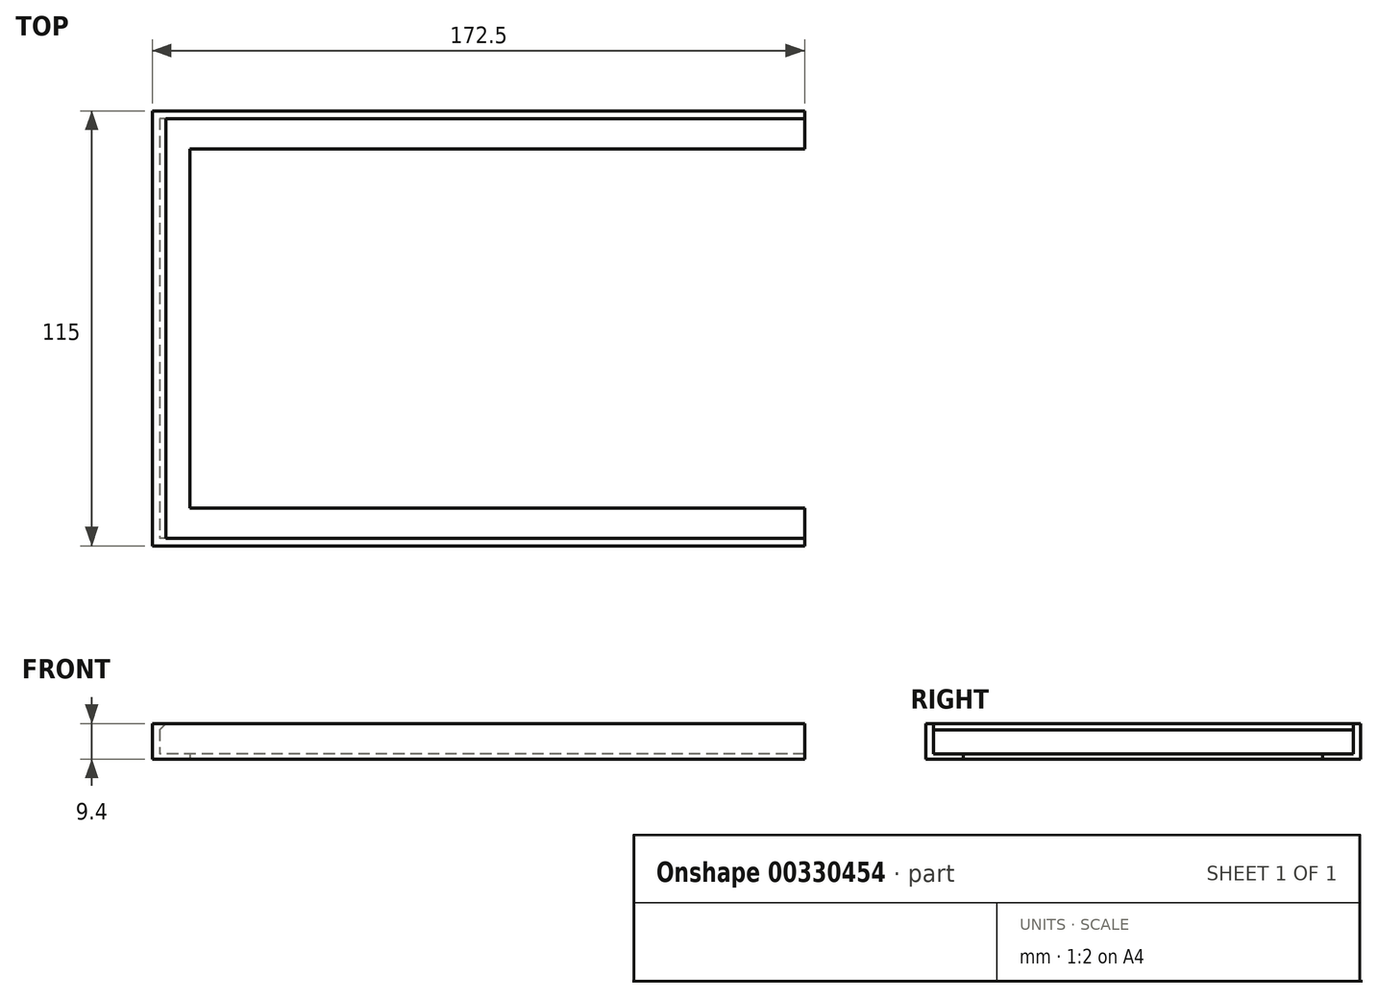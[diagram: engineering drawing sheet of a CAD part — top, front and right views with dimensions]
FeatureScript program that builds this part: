
annotation { "Feature Type Name" : "Feature", "Feature Type Description" : "" }
export const myFeature = defineFeature(function(context is Context, id is Id, definition is map)
    precondition{}
    {
        {
            var Q0;
            Q0=qCreatedBy(makeId("Top.planeOp"),FACE);
            var sketch = newSketch(context, id + "F0", { "sketchPlane" : qUnion([Q0])});
            skLineSegment(sketch, "E0.bottom", {"start": v(86.25, 57.5) * mm, "end": v(-86.25, 57.5) * mm});
            skLineSegment(sketch, "E0.top", {"start": v(86.25, -57.5) * mm, "end": v(-86.25, -57.5) * mm});
            skLineSegment(sketch, "E0.left", {"start": v(86.25, 57.5) * mm, "end": v(86.25, -57.5) * mm});
            skLineSegment(sketch, "E0.right", {"start": v(-86.25, 57.5) * mm, "end": v(-86.25, -57.5) * mm});
            skPoint(sketch, "E0.middle", {"position": v(0, 0) * mm});
            skLineSegment(sketch, "E1.0", {"start": v(86.25, -47.5) * mm, "end": v(-76.25, -47.5) * mm});
            skLineSegment(sketch, "E1.1", {"start": v(-76.25, 47.5) * mm, "end": v(-76.25, -47.5) * mm});
            skLineSegment(sketch, "E1.2", {"start": v(86.25, 47.5) * mm, "end": v(-76.25, 47.5) * mm});
            skLineSegment(sketch, "E2.bottom", {"start": v(-16.25, -47.5) * mm, "end": v(-11.25, -47.5) * mm});
            skLineSegment(sketch, "E2.top", {"start": v(-16.25, 47.5) * mm, "end": v(-11.25, 47.5) * mm});
            skLineSegment(sketch, "E2.left", {"start": v(-16.25, -47.5) * mm, "end": v(-16.25, 47.5) * mm});
            skLineSegment(sketch, "E2.right", {"start": v(-11.25, -47.5) * mm, "end": v(-11.25, 47.5) * mm});
            skLineSegment(sketch, "E3.bottom", {"start": v(48.75, -47.5) * mm, "end": v(53.75, -47.5) * mm});
            skLineSegment(sketch, "E3.top", {"start": v(48.75, 47.5) * mm, "end": v(53.75, 47.5) * mm});
            skLineSegment(sketch, "E3.left", {"start": v(48.75, -47.5) * mm, "end": v(48.75, 47.5) * mm});
            skLineSegment(sketch, "E3.right", {"start": v(53.75, -47.5) * mm, "end": v(53.75, 47.5) * mm});
            skSolve(sketch);
        }
        {
            var Q0;
            {var subQ3=sQuery(id+"F0.wireOp",EDGE,"E0.bottom");Q0=makeQuery(id+"F0.imprint","IMPRINT",FACE,{"disambiguationData":[TD([[makeQuery(id+"F0.imprint","IMPRINT",EDGE,{"derivedFrom":subQ3}),1.0]])]});}
            var Q1;
            Q1=makeQuery(id+"F0.imprint","IMPRINT",FACE,{"disambiguationData":[TD([[makeQuery(id+"F0.imprint","IMPRINT",EDGE,{"derivedFrom":sQuery(id+"F0.wireOp",EDGE,"E2.bottom")}),1.0]])]});
            var Q2;
            Q2=makeQuery(id+"F0.imprint","IMPRINT",FACE,{"disambiguationData":[TD([[makeQuery(id+"F0.imprint","IMPRINT",EDGE,{"derivedFrom":sQuery(id+"F0.wireOp",EDGE,"E3.bottom")}),1.0]])]});
            extrude(context, id + "F1", {"entities" : qUnion([Q0, Q1, Q2]), "depth" : 1.4 * mm, "offsetDistance" : 25 * mm});
        }
        {
            var Q0;
            Q0=makeQuery(id+"F1.opExtrude","CAP_FACE",FACE,{"disambiguationData":[OSD([sQuery(id+"F0.wireOp",EDGE,"E0.bottom"),sQuery(id+"F0.wireOp",EDGE,"E0.top"),sQuery(id+"F0.wireOp",EDGE,"E0.left"),sQuery(id+"F0.wireOp",EDGE,"E0.right"),sQuery(id+"F0.wireOp",EDGE,"E1.0"),sQuery(id+"F0.wireOp",EDGE,"E1.1"),sQuery(id+"F0.wireOp",EDGE,"E1.2")])],"isStart":false});
            var sketch = newSketch(context, id + "F2", { "sketchPlane" : qUnion([Q0])});
            skLineSegment(sketch, "E4.0", {"start": v(86.25, -55.5) * mm, "end": v(-84.25, -55.5) * mm});
            skLineSegment(sketch, "E4.1", {"start": v(-84.25, 55.5) * mm, "end": v(-84.25, -55.5) * mm});
            skLineSegment(sketch, "E4.2", {"start": v(86.25, 55.5) * mm, "end": v(-84.25, 55.5) * mm});
            skSolve(sketch);
        }
        {
            var Q0;
            {var subQ3=sQuery(id+"F2.wireOp",EDGE,"E4.0");Q0=makeQuery(id+"F2.imprint","IMPRINT",FACE,{"disambiguationData":[TD([[makeQuery(id+"F2.imprint","IMPRINT",EDGE,{"derivedFrom":subQ3}),1.0]])]});}
            extrude(context, id + "F3", {"entities" : qUnion([Q0]), "operationType" : NewBodyOperationType.ADD, "depth" : 8 * mm, "offsetDistance" : 25 * mm});
        }
        {
            var Q0;
            Q0=makeQuery(id+"F3.opExtrude","SWEPT_FACE",FACE,{"disambiguationData":[OSD([sQuery(id+"F2.wireOp",EDGE,"E4.2")])]});
            var sketch = newSketch(context, id + "F4", { "sketchPlane" : qUnion([Q0])});
            skLineSegment(sketch, "E5", {"start": v(-84.25, 7.74) * mm, "end": v(-82.63, 9.4) * mm});
            skSolve(sketch);
        }
        {
            var Q0;
            Q0 = qSketchRegion(id + "F4", true);
            var Q1;
            {var subQ0=sQuery(id+"F4.wireOp",EDGE,"E5");Q1=makeQuery(id+"F4.imprint","IMPRINT",FACE,{"disambiguationData":[TD([[makeQuery(id+"F4.imprint","IMPRINT",EDGE,{"derivedFrom":subQ0}),1.0]])]});}
            extrude(context, id + "F5", {"entities" : qUnion([Q0, Q1]), "operationType" : NewBodyOperationType.ADD, "endBound" : BoundingType.UP_TO_NEXT, "depth" : 25 * mm, "offsetDistance" : 25 * mm});
        }
    });
